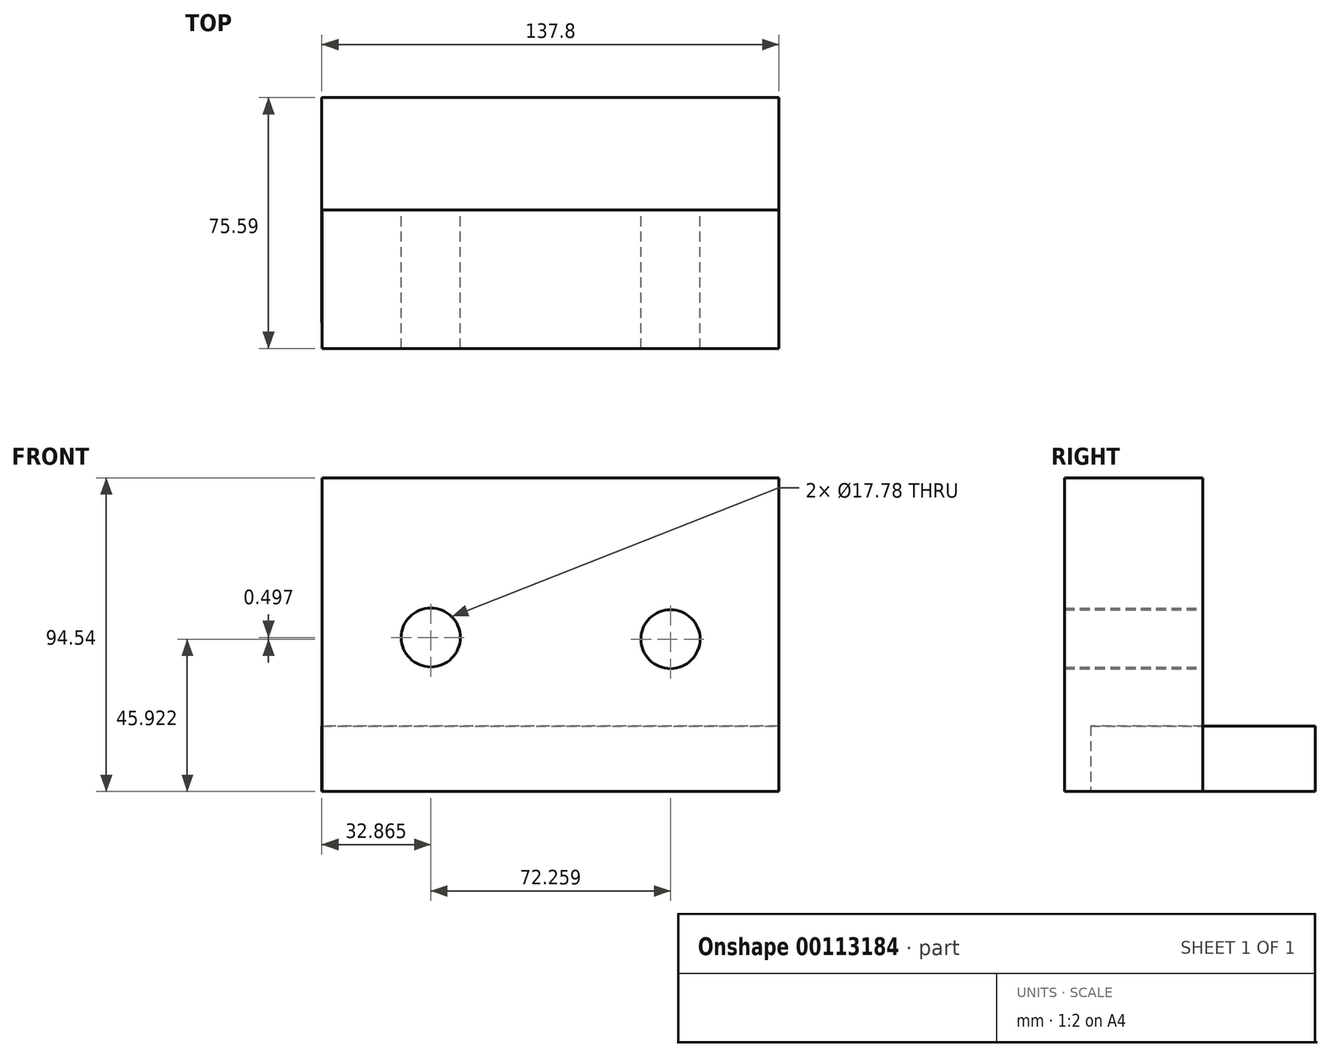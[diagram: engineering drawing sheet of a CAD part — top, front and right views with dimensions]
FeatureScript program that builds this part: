
annotation { "Feature Type Name" : "Feature", "Feature Type Description" : "" }
export const myFeature = defineFeature(function(context is Context, id is Id, definition is map)
    precondition{}
    {
        {
            var Q0;
            Q0=qCreatedBy(makeId("Top.planeOp"),FACE);
            var sketch = newSketch(context, id + "F0", { "sketchPlane" : qUnion([Q0])});
            skLineSegment(sketch, "E0.bottom", {"start": v(68.87, -33.9) * mm, "end": v(-68.87, -33.9) * mm});
            skLineSegment(sketch, "E0.top", {"start": v(68.87, 33.9) * mm, "end": v(-68.87, 33.9) * mm});
            skLineSegment(sketch, "E0.left", {"start": v(68.87, -33.9) * mm, "end": v(68.87, 33.9) * mm});
            skLineSegment(sketch, "E0.right", {"start": v(-68.87, -33.9) * mm, "end": v(-68.87, 33.9) * mm});
            skPoint(sketch, "E0.middle", {"position": v(0, 0) * mm});
            skSolve(sketch);
        }
        {
            var Q0;
            Q0=qCreatedBy(makeId("Front.planeOp"),FACE);
            var sketch = newSketch(context, id + "F1", { "sketchPlane" : qUnion([Q0])});
            skLineSegment(sketch, "E1.bottom", {"start": v(-68.7, 0) * mm, "end": v(68.93, 0) * mm});
            skLineSegment(sketch, "E1.top", {"start": v(-68.7, 94.54) * mm, "end": v(68.93, 94.54) * mm});
            skLineSegment(sketch, "E1.left", {"start": v(-68.7, 0) * mm, "end": v(-68.7, 94.54) * mm});
            skLineSegment(sketch, "E1.right", {"start": v(68.93, 0) * mm, "end": v(68.93, 94.54) * mm});
            skSolve(sketch);
        }
        {
            var Q0;
            Q0=makeQuery(id+"F0.imprint","IMPRINT",FACE,{"disambiguationData":[TD([[makeQuery(id+"F0.imprint","IMPRINT",EDGE,{"derivedFrom":sQuery(id+"F0.wireOp",EDGE,"E0.bottom")}),-1.0]])]});
            extrude(context, id + "F2", {"entities" : qUnion([Q0]), "depth" : 19.76 * mm});
        }
        {
            var Q0;
            Q0=makeQuery(id+"F1.imprint","IMPRINT",FACE,{"disambiguationData":[TD([[makeQuery(id+"F1.imprint","IMPRINT",EDGE,{"derivedFrom":sQuery(id+"F1.wireOp",EDGE,"E1.bottom")}),1.0]])]});
            extrude(context, id + "F3", {"entities" : qUnion([Q0]), "operationType" : NewBodyOperationType.ADD, "depth" : 41.7 * mm});
        }
        {
            var Q0;
            Q0=qCreatedBy(makeId("Front.planeOp"),FACE);
            var sketch = newSketch(context, id + "F4", { "sketchPlane" : qUnion([Q0])});
            skCircle(sketch, "E2", {"center": v(-36, 46.42) * mm, "radius": 9.52 * mm});
            skCircle(sketch, "E3", {"center": v(36.25, 45.92) * mm, "radius": 9.13 * mm});
            skSolve(sketch);
        }
        {
            var Q0;
            Q0=sQuery(id+"F4.wireOp",VERTEX,"E2.center");
            var Q1;
            Q1=sQuery(id+"F4.wireOp",VERTEX,"E3.center");
            var Q2;
            Q2=makeQuery(id+"F2.opExtrude","SWEPT_BODY",BODY,{"disambiguationData":[OSD([sQuery(id+"F0.wireOp",EDGE,"E0.bottom"),sQuery(id+"F0.wireOp",EDGE,"E0.top"),sQuery(id+"F0.wireOp",EDGE,"E0.left"),sQuery(id+"F0.wireOp",EDGE,"E0.right")])]});
            hole(context, id + "F5", {"style" : HoleStyle.SIMPLE, "endStyle" : HoleEndStyle.THROUGH, "oppositeDirection" : true, "holeDiameter" : 17.78 * mm, "locations" : qUnion([Q0, Q1]), "scope" : qUnion([Q2]), "isTappedThrough" : true});
        }
    });
